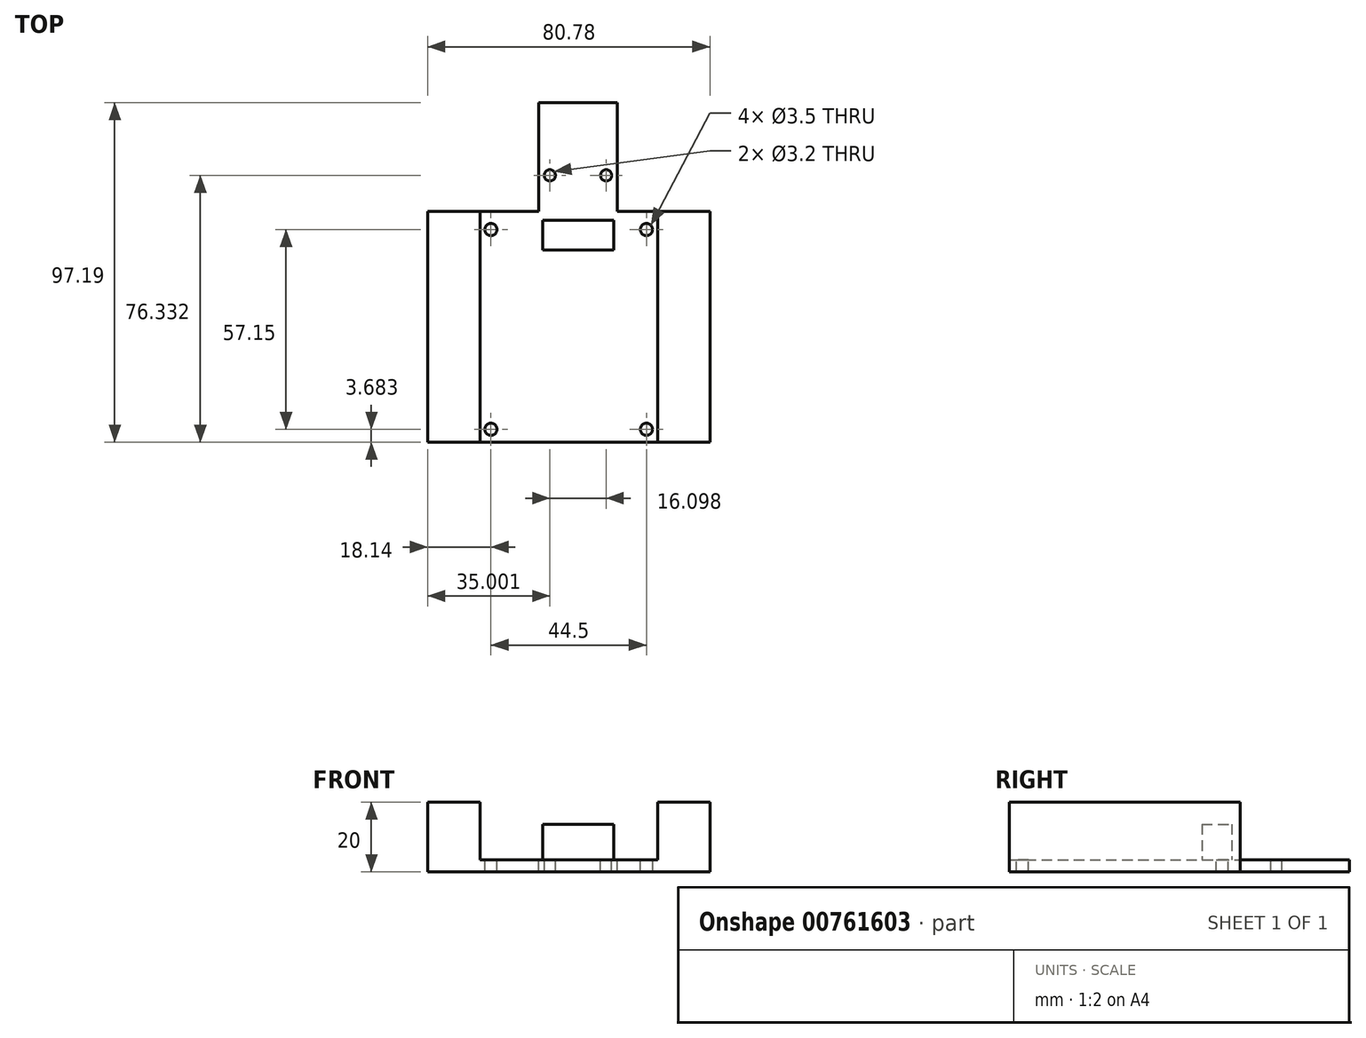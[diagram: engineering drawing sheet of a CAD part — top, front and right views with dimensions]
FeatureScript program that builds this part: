
annotation { "Feature Type Name" : "Feature", "Feature Type Description" : "" }
export const myFeature = defineFeature(function(context is Context, id is Id, definition is map)
    precondition{}
    {
        {
            var Q0;
            Q0=qCreatedBy(makeId("Top.planeOp"),FACE);
            var sketch = newSketch(context, id + "F0", { "sketchPlane" : qUnion([Q0])});
            skLineSegment(sketch, "E0.bottom", {"start": v(25.4, -33.02) * mm, "end": v(-25.4, -33.02) * mm});
            skLineSegment(sketch, "E0.top", {"start": v(25.4, 33.02) * mm, "end": v(-25.4, 33.02) * mm});
            skLineSegment(sketch, "E0.left", {"start": v(25.4, -33.02) * mm, "end": v(25.4, 33.02) * mm});
            skLineSegment(sketch, "E0.right", {"start": v(-25.4, -33.02) * mm, "end": v(-25.4, 33.02) * mm});
            skPoint(sketch, "E0.middle", {"position": v(0, 0) * mm});
            skSolve(sketch);
        }
        {
            var Q0;
            Q0 = qSketchRegion(id + "F0", true);
            extrude(context, id + "F1", {"entities" : qUnion([Q0]), "depth" : 3.5 * mm, "offsetDistance" : 25 * mm});
        }
        {
            var Q0;
            Q0=makeQuery(id+"F1.opExtrude","CAP_FACE",FACE,{"disambiguationData":[OSD([sQuery(id+"F0.wireOp",EDGE,"E0.bottom"),sQuery(id+"F0.wireOp",EDGE,"E0.top"),sQuery(id+"F0.wireOp",EDGE,"E0.left"),sQuery(id+"F0.wireOp",EDGE,"E0.right")])],"isStart":false});
            var sketch = newSketch(context, id + "F2", { "sketchPlane" : qUnion([Q0])});
            skCircle(sketch, "E1", {"center": v(-22.25, 27.81) * mm, "radius": 1.75 * mm});
            skCircle(sketch, "E2", {"center": v(-22.25, -29.34) * mm, "radius": 1.75 * mm});
            skCircle(sketch, "E3", {"center": v(22.25, 27.81) * mm, "radius": 1.75 * mm});
            skCircle(sketch, "E4", {"center": v(22.25, -29.34) * mm, "radius": 1.75 * mm});
            skLineSegment(sketch, "E5", {"start": v(-22.25, -29.34) * mm, "end": v(22.25, -29.34) * mm, "construction": true});
            skLineSegment(sketch, "E6", {"start": v(0, -0.72) * mm, "end": v(0, -29.34) * mm, "construction": true});
            skLineSegment(sketch, "E7", {"start": v(-22.25, 27.81) * mm, "end": v(22.25, 27.81) * mm, "construction": true});
            skLineSegment(sketch, "E8", {"start": v(0, -0.72) * mm, "end": v(0, 27.81) * mm, "construction": true});
            skLineSegment(sketch, "E9", {"start": v(-22.25, 27.81) * mm, "end": v(-22.25, -29.34) * mm, "construction": true});
            skSolve(sketch);
        }
        {
            var Q0;
            Q0 = qSketchRegion(id + "F2", true);
            extrude(context, id + "F3", {"entities" : qUnion([Q0]), "operationType" : NewBodyOperationType.REMOVE, "oppositeDirection" : true, "depth" : 25 * mm, "offsetDistance" : 25 * mm});
        }
        {
            var Q0;
            Q0=makeQuery(id+"F1.opExtrude","CAP_FACE",FACE,{"disambiguationData":[OSD([sQuery(id+"F0.wireOp",EDGE,"E0.bottom"),sQuery(id+"F0.wireOp",EDGE,"E0.top"),sQuery(id+"F0.wireOp",EDGE,"E0.left"),sQuery(id+"F0.wireOp",EDGE,"E0.right")])],"isStart":false});
            var sketch = newSketch(context, id + "F4", { "sketchPlane" : qUnion([Q0])});
            skLineSegment(sketch, "E10", {"start": v(-7.5, 30.52) * mm, "end": v(12.82, 30.52) * mm});
            skLineSegment(sketch, "E11", {"start": v(12.82, 30.52) * mm, "end": v(12.82, 22.01) * mm});
            skLineSegment(sketch, "E12", {"start": v(12.82, 22.01) * mm, "end": v(-7.5, 22.01) * mm});
            skLineSegment(sketch, "E13", {"start": v(-7.5, 22.01) * mm, "end": v(-7.5, 30.52) * mm});
            skSolve(sketch);
        }
        {
            var Q0;
            Q0 = qSketchRegion(id + "F4", true);
            extrude(context, id + "F5", {"entities" : qUnion([Q0]), "operationType" : NewBodyOperationType.ADD, "depth" : 10.16 * mm, "offsetDistance" : 25 * mm});
        }
        {
            var Q0;
            Q0=makeQuery(id+"F1.opExtrude","CAP_FACE",FACE,{"disambiguationData":[OSD([sQuery(id+"F0.wireOp",EDGE,"E0.bottom"),sQuery(id+"F0.wireOp",EDGE,"E0.top"),sQuery(id+"F0.wireOp",EDGE,"E0.left"),sQuery(id+"F0.wireOp",EDGE,"E0.right")])],"isStart":true});
            var sketch = newSketch(context, id + "F6", { "sketchPlane" : qUnion([Q0])});
            skLineSegment(sketch, "E14.bottom", {"start": v(25.4, 33.02) * mm, "end": v(40.39, 33.02) * mm});
            skLineSegment(sketch, "E14.top", {"start": v(25.4, -33.02) * mm, "end": v(40.39, -33.02) * mm});
            skLineSegment(sketch, "E14.left", {"start": v(25.4, 33.02) * mm, "end": v(25.4, -33.02) * mm});
            skLineSegment(sketch, "E14.right", {"start": v(40.39, 33.02) * mm, "end": v(40.39, -33.02) * mm});
            skLineSegment(sketch, "E15.MirrorCS", {"start": v(-25.4, 33.02) * mm, "end": v(-25.4, -33.02) * mm});
            skLineSegment(sketch, "E16.MirrorCS", {"start": v(-25.4, 33.02) * mm, "end": v(-40.39, 33.02) * mm});
            skLineSegment(sketch, "E17.MirrorCS", {"start": v(-40.39, 33.02) * mm, "end": v(-40.39, -33.02) * mm});
            skLineSegment(sketch, "E18.MirrorCS", {"start": v(-25.4, -33.02) * mm, "end": v(-40.39, -33.02) * mm});
            skSolve(sketch);
        }
        {
            var Q0;
            Q0 = qSketchRegion(id + "F6", true);
            extrude(context, id + "F7", {"entities" : qUnion([Q0]), "operationType" : NewBodyOperationType.ADD, "oppositeDirection" : true, "depth" : 20 * mm, "offsetDistance" : 25 * mm});
        }
        {
            var Q0;
            Q0=makeQuery(id+"F1.opExtrude","CAP_FACE",FACE,{"disambiguationData":[OSD([sQuery(id+"F0.wireOp",EDGE,"E0.bottom"),sQuery(id+"F0.wireOp",EDGE,"E0.top"),sQuery(id+"F0.wireOp",EDGE,"E0.left"),sQuery(id+"F0.wireOp",EDGE,"E0.right")])],"isStart":false});
            var sketch = newSketch(context, id + "F8", { "sketchPlane" : qUnion([Q0])});
            skLineSegment(sketch, "E19", {"start": v(2.66, 30.52) * mm, "end": v(2.66, 64.17) * mm, "construction": true});
            skLineSegment(sketch, "E20", {"start": v(2.66, 64.17) * mm, "end": v(13.88, 64.17) * mm});
            skLineSegment(sketch, "E21", {"start": v(2.66, 64.17) * mm, "end": v(-8.56, 64.17) * mm});
            skLineSegment(sketch, "E22", {"start": v(-8.56, 64.17) * mm, "end": v(-8.56, 33.02) * mm});
            skLineSegment(sketch, "E23", {"start": v(13.88, 64.17) * mm, "end": v(13.88, 33.02) * mm});
            skLineSegment(sketch, "E24", {"start": v(-8.56, 33.02) * mm, "end": v(13.88, 33.02) * mm});
            skSolve(sketch);
        }
        {
            var Q0;
            Q0 = qSketchRegion(id + "F8", true);
            var Q1;
            Q1=makeQuery(id+"F7.boolean.opBoolean","MERGE",FACE,{"derivedFrom":[makeQuery(id+"F1.opExtrude","CAP_FACE",FACE,{"disambiguationData":[OSD([sQuery(id+"F0.wireOp",EDGE,"E0.bottom"),sQuery(id+"F0.wireOp",EDGE,"E0.top"),sQuery(id+"F0.wireOp",EDGE,"E0.left"),sQuery(id+"F0.wireOp",EDGE,"E0.right")])],"isStart":true}),makeQuery(id+"F7.opExtrude","CAP_FACE",FACE,{"disambiguationData":[OSD([sQuery(id+"F6.wireOp",EDGE,"E14.bottom"),sQuery(id+"F6.wireOp",EDGE,"E14.top"),sQuery(id+"F6.wireOp",EDGE,"E14.left"),sQuery(id+"F6.wireOp",EDGE,"E14.right")])],"isStart":true}),makeQuery(id+"F7.opExtrude","CAP_FACE",FACE,{"disambiguationData":[OSD([sQuery(id+"F6.wireOp",EDGE,"E15.MirrorCS"),sQuery(id+"F6.wireOp",EDGE,"E16.MirrorCS"),sQuery(id+"F6.wireOp",EDGE,"E17.MirrorCS"),sQuery(id+"F6.wireOp",EDGE,"E18.MirrorCS")])],"isStart":true})]});
            extrude(context, id + "F9", {"entities" : qUnion([Q0]), "operationType" : NewBodyOperationType.ADD, "endBound" : BoundingType.UP_TO_SURFACE, "oppositeDirection" : true, "depth" : 25 * mm, "endBoundEntityFace" : qUnion([Q1]), "offsetDistance" : 25 * mm});
        }
        {
            var Q0;
            Q0=makeQuery(id+"F9.boolean.opBoolean","MERGE",FACE,{"derivedFrom":[makeQuery(id+"F1.opExtrude","CAP_FACE",FACE,{"disambiguationData":[OSD([sQuery(id+"F0.wireOp",EDGE,"E0.bottom"),sQuery(id+"F0.wireOp",EDGE,"E0.top"),sQuery(id+"F0.wireOp",EDGE,"E0.left"),sQuery(id+"F0.wireOp",EDGE,"E0.right")])],"isStart":false}),makeQuery(id+"F9.opExtrude","CAP_FACE",FACE,{"disambiguationData":[OSD([sQuery(id+"F8.wireOp",EDGE,"E20"),sQuery(id+"F8.wireOp",EDGE,"E21"),sQuery(id+"F8.wireOp",EDGE,"E22"),sQuery(id+"F8.wireOp",EDGE,"E23"),sQuery(id+"F8.wireOp",EDGE,"E24")])],"isStart":true})]});
            var sketch = newSketch(context, id + "F10", { "sketchPlane" : qUnion([Q0])});
            skCircle(sketch, "E25", {"center": v(-5.39, 43.31) * mm, "radius": 1.6 * mm});
            skLineSegment(sketch, "E26", {"start": v(2.66, 30.52) * mm, "end": v(2.66, 62.9) * mm, "construction": true});
            skCircle(sketch, "E27.MirrorC", {"center": v(10.7, 43.31) * mm, "radius": 1.6 * mm});
            skSolve(sketch);
        }
        {
            var Q0;
            Q0 = qSketchRegion(id + "F10", true);
            var Q1;
            Q1=makeQuery(id+"F1.opExtrude","SWEPT_BODY",BODY,{"disambiguationData":[OSD([sQuery(id+"F0.wireOp",EDGE,"E0.bottom"),sQuery(id+"F0.wireOp",EDGE,"E0.top"),sQuery(id+"F0.wireOp",EDGE,"E0.left"),sQuery(id+"F0.wireOp",EDGE,"E0.right")])]});
            extrude(context, id + "F11", {"entities" : qUnion([Q0]), "operationType" : NewBodyOperationType.REMOVE, "endBound" : BoundingType.UP_TO_BODY, "oppositeDirection" : true, "depth" : 25 * mm, "endBoundEntityBody" : qUnion([Q1]), "offsetDistance" : 25 * mm});
        }
    });
